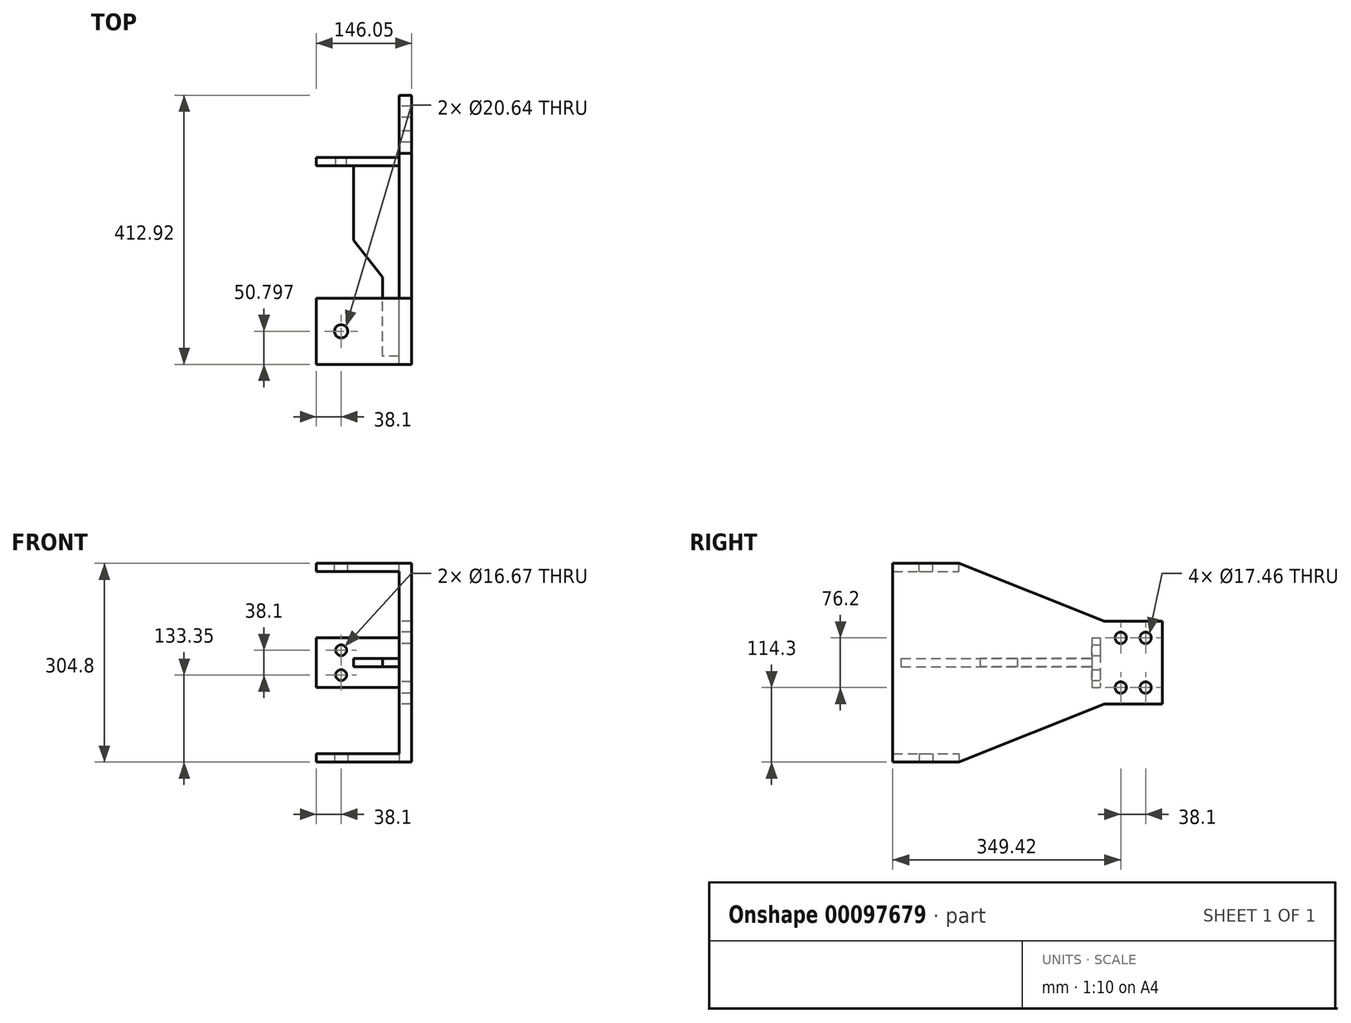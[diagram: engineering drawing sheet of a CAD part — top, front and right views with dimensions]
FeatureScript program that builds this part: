
annotation { "Feature Type Name" : "Feature", "Feature Type Description" : "" }
export const myFeature = defineFeature(function(context is Context, id is Id, definition is map)
    precondition{}
    {
        {
            var Q0;
            Q0=qCreatedBy(makeId("Right.planeOp"),FACE);
            var sketch = newSketch(context, id + "F0", { "sketchPlane" : qUnion([Q0])});
            skLineSegment(sketch, "E0.bottom", {"start": v(-44.45, 63.5) * mm, "end": v(44.45, 63.5) * mm});
            skLineSegment(sketch, "E0.top", {"start": v(-44.45, -63.5) * mm, "end": v(44.45, -63.5) * mm});
            skLineSegment(sketch, "E0.right", {"start": v(44.45, 63.5) * mm, "end": v(44.45, -63.5) * mm});
            skPoint(sketch, "E0.middle", {"position": v(0, 0) * mm});
            skLineSegment(sketch, "E1", {"start": v(0, 91.72) * mm, "end": v(0, -93.08) * mm, "construction": true});
            skLineSegment(sketch, "E2", {"start": v(91.72, 0) * mm, "end": v(-89.7, 0) * mm, "construction": true});
            skPoint(sketch, "E2.endSnap0", {"position": v(-44.45, 0) * mm});
            skLineSegment(sketch, "E3.0", {"start": v(-19.05, 93.08) * mm, "end": v(-19.05, -93.08) * mm, "construction": true});
            skLineSegment(sketch, "E4.0", {"start": v(91.72, 38.1) * mm, "end": v(-89.7, 38.1) * mm, "construction": true});
            skCircle(sketch, "E5", {"center": v(-19.05, 38.1) * mm, "radius": 8.73 * mm});
            skCircle(sketch, "E6.0.1.0", {"center": v(-19.05, -38.1) * mm, "radius": 8.73 * mm});
            skCircle(sketch, "E6.1.0.0", {"center": v(19.05, 38.1) * mm, "radius": 8.73 * mm});
            skCircle(sketch, "E6.1.1.0", {"center": v(19.05, -38.1) * mm, "radius": 8.73 * mm});
            skLineSegment(sketch, "E6.direction1", {"start": v(-19.05, 38.1) * mm, "end": v(19.05, 38.1) * mm, "construction": true});
            skLineSegment(sketch, "E6.direction2", {"start": v(-19.05, 38.1) * mm, "end": v(-19.05, -38.1) * mm, "construction": true});
            skLineSegment(sketch, "E7.0", {"start": v(-368.47, 152.4) * mm, "end": v(-368.47, -152.4) * mm});
            skLineSegment(sketch, "E8", {"start": v(111.82, 0) * mm, "end": v(-44.52, 0) * mm, "construction": true});
            skPoint(sketch, "E8.startSnap0", {"position": v(-19.05, 0) * mm});
            skLineSegment(sketch, "E9.0", {"start": v(111.82, 152.4) * mm, "end": v(-482.27, 152.4) * mm, "construction": true});
            skLineSegment(sketch, "E10.0", {"start": v(-266.87, 152.4) * mm, "end": v(-266.87, 152.4) * mm});
            skLineSegment(sketch, "E11", {"start": v(-368.47, 152.4) * mm, "end": v(-266.87, 152.4) * mm});
            skLineSegment(sketch, "E12", {"start": v(-44.45, 63.5) * mm, "end": v(-266.87, 152.4) * mm});
            skLineSegment(sketch, "E13.MirrorCS", {"start": v(-368.47, -152.4) * mm, "end": v(-266.87, -152.4) * mm});
            skLineSegment(sketch, "E14.MirrorCS", {"start": v(-44.45, -63.5) * mm, "end": v(-266.87, -152.4) * mm});
            skLineSegment(sketch, "E15.trimOffspring", {"start": v(-44.45, 0) * mm, "end": v(-44.45, 0) * mm});
            skSolve(sketch);
        }
        {
            var Q0;
            Q0 = qSketchRegion(id + "F0", true);
            extrude(context, id + "F1", {"entities" : qUnion([Q0]), "depth" : 19.05 * mm});
        }
        {
            var Q0;
            Q0=makeQuery(id+"F1.opExtrude","SWEPT_FACE",FACE,{"disambiguationData":[OSD([sQuery(id+"F0.wireOp",EDGE,"E11")])]});
            var sketch = newSketch(context, id + "F2", { "sketchPlane" : qUnion([Q0])});
            skLineSegment(sketch, "E16.bottom", {"start": v(0, -368.47) * mm, "end": v(-127, -368.47) * mm});
            skLineSegment(sketch, "E16.top", {"start": v(0, -266.87) * mm, "end": v(-127, -266.87) * mm});
            skLineSegment(sketch, "E16.left", {"start": v(0, -368.47) * mm, "end": v(0, -266.87) * mm});
            skLineSegment(sketch, "E16.right", {"start": v(-127, -368.47) * mm, "end": v(-127, -266.87) * mm});
            skLineSegment(sketch, "E17.0", {"start": v(-88.9, -368.47) * mm, "end": v(-88.9, -266.87) * mm, "construction": true});
            skCircle(sketch, "E18", {"center": v(-88.9, -317.67) * mm, "radius": 10.32 * mm});
            skSolve(sketch);
        }
        {
            var Q0;
            Q0 = qSketchRegion(id + "F2", true);
            extrude(context, id + "F3", {"entities" : qUnion([Q0]), "oppositeDirection" : true, "depth" : 12.7 * mm});
        }
        {
            var Q0;
            Q0=makeQuery(id+"F3.opExtrude","SWEPT_BODY",BODY,{"disambiguationData":[OSD([sQuery(id+"F2.wireOp",EDGE,"E16.bottom"),sQuery(id+"F2.wireOp",EDGE,"E16.top"),sQuery(id+"F2.wireOp",EDGE,"E16.left"),sQuery(id+"F2.wireOp",EDGE,"E16.right"),sQuery(id+"F2.wireOp",EDGE,"E18")])]});
            var Q1;
            Q1=qCreatedBy(makeId("Top.planeOp"),FACE);
            mirror(context, id + "F4", {"operationType" : NewBodyOperationType.ADD, "entities" : qUnion([Q0]), "mirrorPlane" : qUnion([Q1])});
        }
        {
            var Q0;
            Q0=qCreatedBy(makeId("Top.planeOp"),FACE);
            var sketch = newSketch(context, id + "F5", { "sketchPlane" : qUnion([Q0])});
            skCircle(sketch, "E19.0", {"center": v(-88.9, -317.67) * mm, "radius": 10.32 * mm, "construction": true});
            skLineSegment(sketch, "E20", {"start": v(-88.9, -317.67) * mm, "end": v(140.51, -317.67) * mm, "construction": true});
            skLineSegment(sketch, "E21.0", {"start": v(-88.9, -355.77) * mm, "end": v(140.51, -355.77) * mm, "construction": true});
            skLineSegment(sketch, "E22.0", {"start": v(-25.4, -44.45) * mm, "end": v(-25.4, -266.87) * mm, "construction": true});
            skLineSegment(sketch, "E23.0", {"start": v(0, -368.47) * mm, "end": v(0, -266.87) * mm, "construction": true});
            skLineSegment(sketch, "E24.bottom", {"start": v(0, -355.77) * mm, "end": v(-25.4, -355.77) * mm});
            skLineSegment(sketch, "E24.top", {"start": v(0, -234.5) * mm, "end": v(-25.4, -234.5) * mm});
            skLineSegment(sketch, "E24.left", {"start": v(0, -355.77) * mm, "end": v(0, -234.5) * mm});
            skLineSegment(sketch, "E24.right", {"start": v(-25.4, -355.77) * mm, "end": v(-25.4, -234.5) * mm});
            skLineSegment(sketch, "E25.0", {"start": v(19.05, 44.45) * mm, "end": v(-178.05, 44.45) * mm, "construction": true});
            skPoint(sketch, "E26.orphan", {"position": v(0, 44.45) * mm});
            skLineSegment(sketch, "E27.0", {"start": v(19.05, -63.5) * mm, "end": v(-178.05, -63.5) * mm, "construction": true});
            skLineSegment(sketch, "E28.0", {"start": v(0, -44.45) * mm, "end": v(0, -266.87) * mm, "construction": true});
            skLineSegment(sketch, "E29.bottom", {"start": v(0, -63.5) * mm, "end": v(-69.85, -63.5) * mm});
            skLineSegment(sketch, "E29.top", {"start": v(0, -177.8) * mm, "end": v(-69.85, -177.8) * mm});
            skLineSegment(sketch, "E29.left", {"start": v(0, -63.5) * mm, "end": v(0, -177.8) * mm});
            skLineSegment(sketch, "E29.right", {"start": v(-69.85, -63.5) * mm, "end": v(-69.85, -177.8) * mm});
            skLineSegment(sketch, "E30", {"start": v(0, -234.5) * mm, "end": v(0, -177.8) * mm});
            skLineSegment(sketch, "E31", {"start": v(-69.85, -177.8) * mm, "end": v(-25.4, -234.5) * mm});
            skSolve(sketch);
        }
        {
            var Q0;
            Q0 = qSketchRegion(id + "F5", true);
            extrude(context, id + "F6", {"entities" : qUnion([Q0]), "operationType" : NewBodyOperationType.ADD, "endBound" : BoundingType.SYMMETRIC, "depth" : 12.7 * mm});
        }
        {
            var Q0;
            Q0=makeQuery(id+"F1.opExtrude","CAP_FACE",FACE,{"disambiguationData":[OSD([sQuery(id+"F0.wireOp",EDGE,"E0.bottom"),sQuery(id+"F0.wireOp",EDGE,"E0.top"),sQuery(id+"F0.wireOp",EDGE,"E0.right"),sQuery(id+"F0.wireOp",EDGE,"E5"),sQuery(id+"F0.wireOp",EDGE,"E6.0.1.0"),sQuery(id+"F0.wireOp",EDGE,"E6.1.0.0"),sQuery(id+"F0.wireOp",EDGE,"E6.1.1.0"),sQuery(id+"F0.wireOp",EDGE,"E7.0"),sQuery(id+"F0.wireOp",EDGE,"E11"),sQuery(id+"F0.wireOp",EDGE,"E12"),sQuery(id+"F0.wireOp",EDGE,"E13.MirrorCS"),sQuery(id+"F0.wireOp",EDGE,"E14.MirrorCS")])],"isStart":true});
            var sketch = newSketch(context, id + "F7", { "sketchPlane" : qUnion([Q0])});
            skLineSegment(sketch, "E32.bottom", {"start": v(63.5, 38.1) * mm, "end": v(50.8, 38.1) * mm});
            skLineSegment(sketch, "E32.top", {"start": v(63.5, -38.1) * mm, "end": v(50.8, -38.1) * mm});
            skLineSegment(sketch, "E32.left", {"start": v(63.5, 38.1) * mm, "end": v(63.5, -38.1) * mm});
            skLineSegment(sketch, "E32.right", {"start": v(50.8, 38.1) * mm, "end": v(50.8, -38.1) * mm});
            skSolve(sketch);
        }
        {
            var Q0;
            Q0 = qSketchRegion(id + "F7", true);
            extrude(context, id + "F8", {"entities" : qUnion([Q0]), "operationType" : NewBodyOperationType.ADD, "depth" : 127 * mm});
        }
        {
            var Q0;
            Q0=makeQuery(id+"F8.opExtrude","SWEPT_FACE",FACE,{"disambiguationData":[OSD([sQuery(id+"F7.wireOp",EDGE,"E32.right")])]});
            var sketch = newSketch(context, id + "F9", { "sketchPlane" : qUnion([Q0])});
            skLineSegment(sketch, "E33.0.0", {"start": v(127, -38.1) * mm, "end": v(127, 38.1) * mm, "construction": true});
            skLineSegment(sketch, "E33.0.2", {"start": v(127, 38.1) * mm, "end": v(127, -38.1) * mm, "construction": true});
            skLineSegment(sketch, "E34.0", {"start": v(88.9, 38.1) * mm, "end": v(88.9, -38.1) * mm, "construction": true});
            skLineSegment(sketch, "E35", {"start": v(88.9, 0) * mm, "end": v(127, 0) * mm, "construction": true});
            skLineSegment(sketch, "E36.0", {"start": v(88.9, 19.05) * mm, "end": v(127, 19.05) * mm, "construction": true});
            skPoint(sketch, "E37", {"position": v(88.9, 19.05) * mm});
            skPoint(sketch, "E38.MirrorP", {"position": v(88.9, -19.05) * mm});
            skSolve(sketch);
        }
        {
            var Q0;
            Q0=sQuery(id+"F9.wireOp",VERTEX,"E37");
            var Q1;
            Q1=sQuery(id+"F9.wireOp",VERTEX,"E38.MirrorP");
            var Q2;
            Q2=makeQuery(id+"F1.opExtrude","SWEPT_BODY",BODY,{"disambiguationData":[OSD([sQuery(id+"F0.wireOp",EDGE,"E0.bottom"),sQuery(id+"F0.wireOp",EDGE,"E0.top"),sQuery(id+"F0.wireOp",EDGE,"E0.right"),sQuery(id+"F0.wireOp",EDGE,"E5"),sQuery(id+"F0.wireOp",EDGE,"E6.0.1.0"),sQuery(id+"F0.wireOp",EDGE,"E6.1.0.0"),sQuery(id+"F0.wireOp",EDGE,"E6.1.1.0"),sQuery(id+"F0.wireOp",EDGE,"E7.0"),sQuery(id+"F0.wireOp",EDGE,"E11"),sQuery(id+"F0.wireOp",EDGE,"E12"),sQuery(id+"F0.wireOp",EDGE,"E13.MirrorCS"),sQuery(id+"F0.wireOp",EDGE,"E14.MirrorCS")])]});
            hole(context, id + "F10", {"style" : HoleStyle.SIMPLE, "endStyle" : HoleEndStyle.THROUGH, "standardTappedOrClearance" : lookupTablePath({ "standard" : "ANSI", "fit" : "Normal (ASME)", "size" : "5/8", "type" : "Clearance" }), "standardBlindInLast" : lookupTablePath({ "fit" : "Free", "standard" : "ANSI", "size" : "5/8", "type" : "Clearance" }), "holeDiameter" : 16.67 * mm, "locations" : qUnion([Q0, Q1]), "scope" : qUnion([Q2]), "isTappedThrough" : true});
        }
    });
